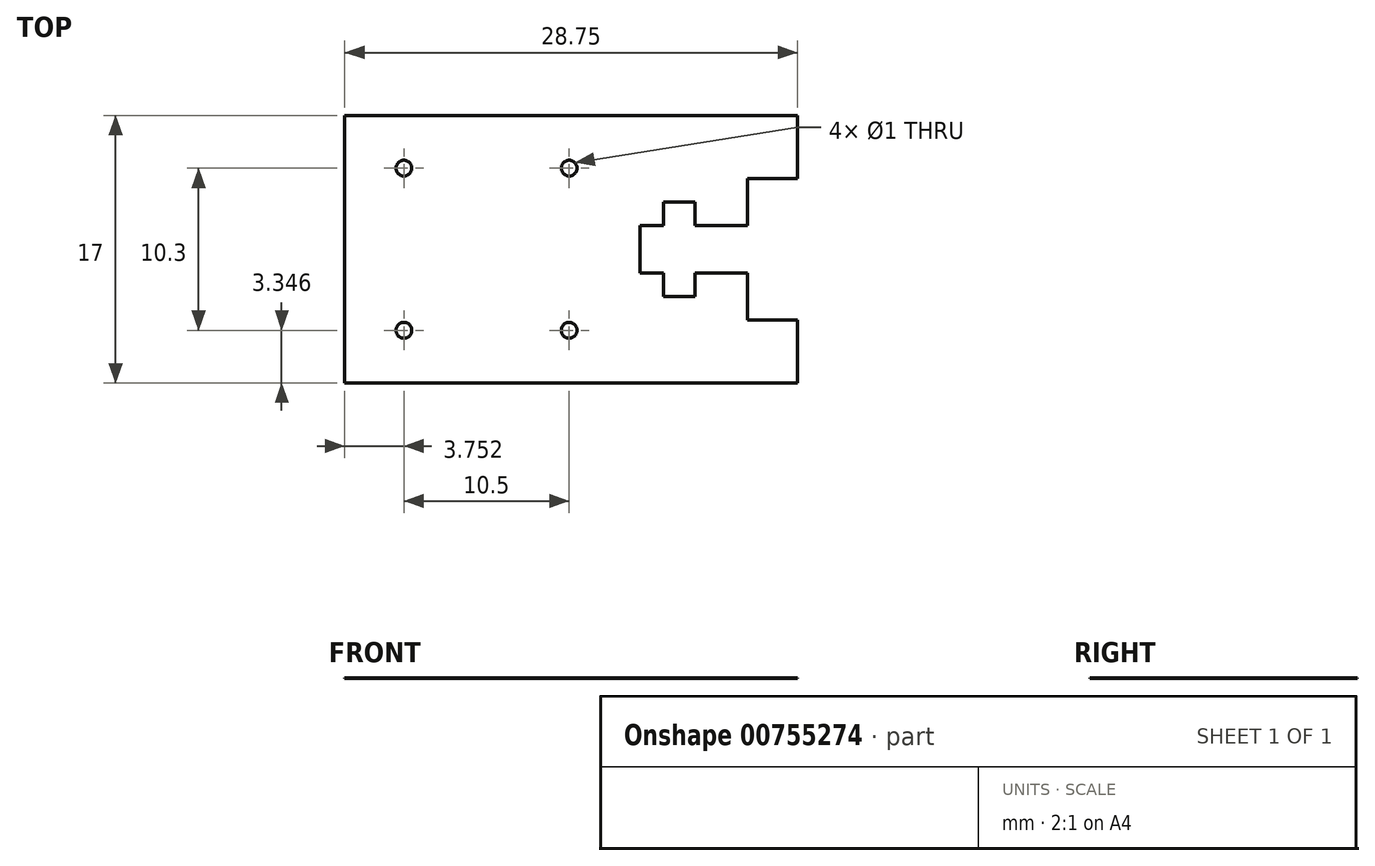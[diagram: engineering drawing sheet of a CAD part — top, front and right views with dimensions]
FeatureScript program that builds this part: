
annotation { "Feature Type Name" : "Feature", "Feature Type Description" : "" }
export const myFeature = defineFeature(function(context is Context, id is Id, definition is map)
    precondition{}
    {
        {
            var Q0;
            Q0=qCreatedBy(makeId("Top.planeOp"),FACE);
            var sketch = newSketch(context, id + "F0", { "sketchPlane" : qUnion([Q0])});
            skLineSegment(sketch, "E0.bottom", {"start": v(38.5, 22.55) * mm, "end": v(40, 22.55) * mm});
            skLineSegment(sketch, "E0.top", {"start": v(38.5, 19.55) * mm, "end": v(40, 19.55) * mm});
            skLineSegment(sketch, "E0.left", {"start": v(38.5, 22.55) * mm, "end": v(38.5, 19.55) * mm});
            skPoint(sketch, "E0.middle", {"position": v(43.5, 21.05) * mm});
            skLineSegment(sketch, "E1.bottom", {"start": v(40, 24.05) * mm, "end": v(42, 24.05) * mm});
            skLineSegment(sketch, "E1.top", {"start": v(40, 18.05) * mm, "end": v(42, 18.05) * mm});
            skLineSegment(sketch, "E1.left", {"start": v(40, 24.05) * mm, "end": v(40, 22.55) * mm});
            skLineSegment(sketch, "E1.right", {"start": v(42, 24.05) * mm, "end": v(42, 22.55) * mm});
            skPoint(sketch, "E1.middle", {"position": v(41, 21.05) * mm});
            skLineSegment(sketch, "E2.bottom", {"start": v(48.5, 29.55) * mm, "end": v(45.33, 29.55) * mm});
            skLineSegment(sketch, "E2.top", {"start": v(48.5, 25.55) * mm, "end": v(45.33, 25.55) * mm});
            skLineSegment(sketch, "E2.left", {"start": v(48.5, 29.55) * mm, "end": v(48.5, 25.55) * mm});
            skLineSegment(sketch, "E3.MirrorCS", {"start": v(48.5, 16.55) * mm, "end": v(45.33, 16.55) * mm});
            skLineSegment(sketch, "E4.MirrorCS", {"start": v(48.5, 12.55) * mm, "end": v(48.5, 16.55) * mm});
            skLineSegment(sketch, "E5.MirrorCS", {"start": v(48.5, 12.55) * mm, "end": v(45.33, 12.55) * mm});
            skCircle(sketch, "E6", {"center": v(23.5, 26.2) * mm, "radius": 0.5 * mm});
            skCircle(sketch, "E7", {"center": v(34, 26.2) * mm, "radius": 0.5 * mm});
            skCircle(sketch, "E8.MirrorC", {"center": v(23.5, 15.9) * mm, "radius": 0.5 * mm});
            skCircle(sketch, "E9.MirrorC", {"center": v(34, 15.9) * mm, "radius": 0.5 * mm});
            skLineSegment(sketch, "E10.bottom", {"start": v(45.33, 29.55) * mm, "end": v(19.75, 29.55) * mm});
            skLineSegment(sketch, "E10.top", {"start": v(45.33, 12.55) * mm, "end": v(19.75, 12.55) * mm});
            skLineSegment(sketch, "E10.left", {"start": v(45.33, 25.55) * mm, "end": v(45.33, 22.55) * mm});
            skLineSegment(sketch, "E10.right", {"start": v(19.75, 29.55) * mm, "end": v(19.75, 12.55) * mm});
            skLineSegment(sketch, "E11.trimOffspring", {"start": v(45.33, 19.55) * mm, "end": v(45.33, 16.55) * mm});
            skPoint(sketch, "E0.right.start.orphan", {"position": v(48.5, 22.55) * mm});
            skPoint(sketch, "E12.orphan", {"position": v(48.5, 19.55) * mm});
            skLineSegment(sketch, "E13.trimOffspring", {"start": v(42, 19.55) * mm, "end": v(42, 18.05) * mm});
            skLineSegment(sketch, "E14.trimOffspring", {"start": v(42, 22.55) * mm, "end": v(45.33, 22.55) * mm});
            skLineSegment(sketch, "E15.trimOffspring", {"start": v(40, 19.55) * mm, "end": v(40, 18.05) * mm});
            skLineSegment(sketch, "E16.trimOffspring", {"start": v(42, 19.55) * mm, "end": v(45.33, 19.55) * mm});
            skPoint(sketch, "E17.orphan", {"position": v(34, 21.05) * mm});
            skPoint(sketch, "E18.start.orphan", {"position": v(23.5, 21.05) * mm});
            skPoint(sketch, "E19.end.orphan", {"position": v(28.75, 26.2) * mm});
            skPoint(sketch, "E19.start.orphan", {"position": v(28.75, 21.05) * mm});
            skSolve(sketch);
        }
        {
            var Q0;
            {var subQ10=sQuery(id+"F0.wireOp",EDGE,"E0.left");Q0=makeQuery(id+"F0.imprint","IMPRINT",FACE,{"disambiguationData":[TD([[makeQuery(id+"F0.imprint","IMPRINT",EDGE,{"derivedFrom":subQ10}),-1.0]])]});}
            var Q1;
            {var subQ0=sQuery(id+"F0.wireOp",EDGE,"E2.bottom");Q1=makeQuery(id+"F0.imprint","IMPRINT",FACE,{"disambiguationData":[TD([[makeQuery(id+"F0.imprint","IMPRINT",EDGE,{"derivedFrom":subQ0}),1.0]])]});}
            var Q2;
            {var subQ0=sQuery(id+"F0.wireOp",EDGE,"E3.MirrorCS");Q2=makeQuery(id+"F0.imprint","IMPRINT",FACE,{"disambiguationData":[TD([[makeQuery(id+"F0.imprint","IMPRINT",EDGE,{"derivedFrom":subQ0}),1.0]])]});}
            extrude(context, id + "F1", {"entities" : qUnion([Q0, Q1, Q2]), "depth" : 1 / 203.2 * mm, "offsetDistance" : 25 * mm});
        }
    });
